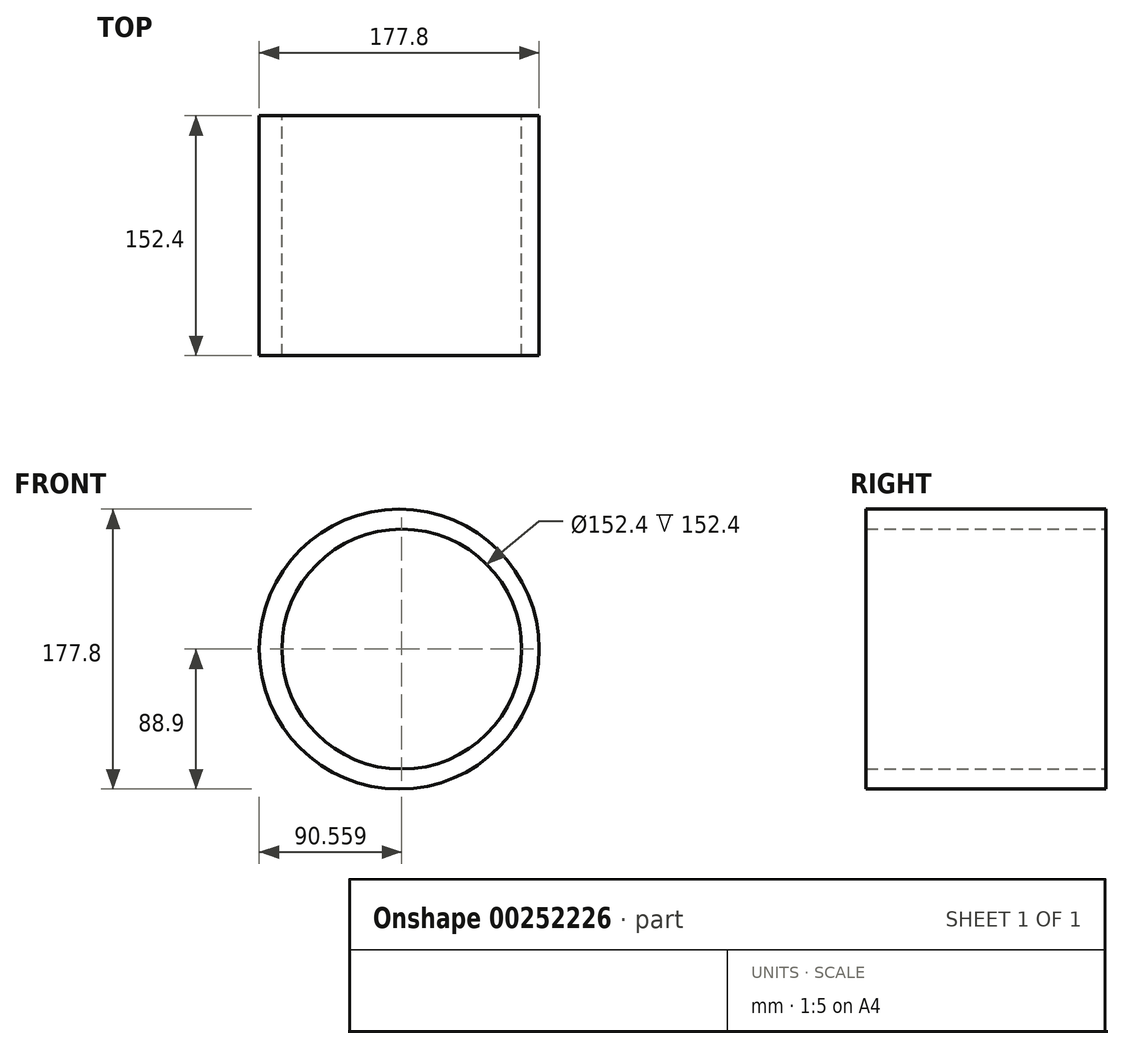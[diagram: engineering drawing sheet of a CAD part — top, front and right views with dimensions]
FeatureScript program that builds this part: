
annotation { "Feature Type Name" : "Feature", "Feature Type Description" : "" }
export const myFeature = defineFeature(function(context is Context, id is Id, definition is map)
    precondition{}
    {
        {
            var Q0;
            Q0=qCreatedBy(makeId("Front.planeOp"),FACE);
            var sketch = newSketch(context, id + "F0", { "sketchPlane" : qUnion([Q0])});
            skCircle(sketch, "E0", {"center": v(0, 0) * mm, "radius": 88.9 * mm});
            skCircle(sketch, "E1", {"center": v(1.66, 0) * mm, "radius": 76.2 * mm});
            skCircle(sketch, "E2", {"center": v(1.66, 0) * mm, "radius": 63.5 * mm});
            skCircle(sketch, "E3", {"center": v(0, 0) * mm, "radius": 50.8 * mm});
            skCircle(sketch, "E4", {"center": v(1.66, 0) * mm, "radius": 38.1 * mm});
            skCircle(sketch, "E5", {"center": v(0, 0) * mm, "radius": 25.4 * mm});
            skCircle(sketch, "E6", {"center": v(0, 0) * mm, "radius": 12.7 * mm});
            skSolve(sketch);
        }
        {
            var Q0;
            Q0=makeQuery(id+"F0.imprint","IMPRINT",FACE,{"disambiguationData":[TD([[makeQuery(id+"F0.imprint","IMPRINT",EDGE,{"derivedFrom":sQuery(id+"F0.wireOp",EDGE,"E0")}),1.0]])]});
            extrude(context, id + "F1", {"entities" : qUnion([Q0]), "endBound" : BoundingType.SYMMETRIC, "depth" : 152.4 * mm});
        }
        {
            var Q0;
            Q0 = qSketchRegion(id + "F0", true);
            extrude(context, id + "F2", {"entities" : qUnion([Q0]), "operationType" : NewBodyOperationType.ADD, "depth" : 25.4 * mm});
        }
    });
